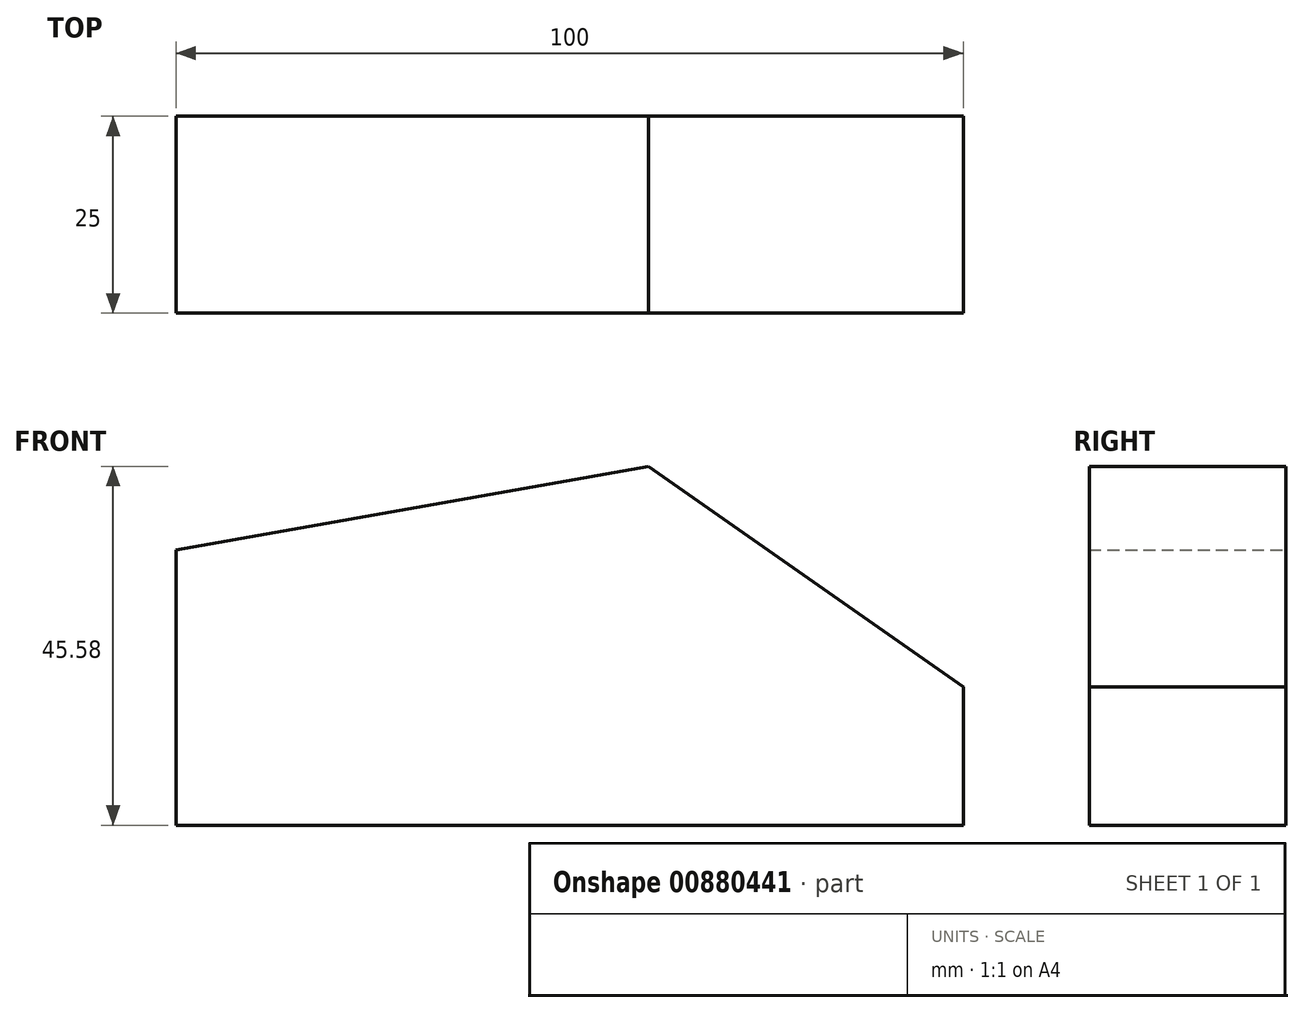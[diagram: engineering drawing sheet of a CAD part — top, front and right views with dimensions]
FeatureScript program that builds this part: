
annotation { "Feature Type Name" : "Feature", "Feature Type Description" : "" }
export const myFeature = defineFeature(function(context is Context, id is Id, definition is map)
    precondition{}
    {
        {
            var Q0;
            Q0=qCreatedBy(makeId("Front.planeOp"),FACE);
            var sketch = newSketch(context, id + "F0", { "sketchPlane" : qUnion([Q0])});
            skLineSegment(sketch, "E0", {"start": v(0, 0) * mm, "end": v(100, 0) * mm});
            skLineSegment(sketch, "E1", {"start": v(100, 0) * mm, "end": v(100, 17.57) * mm});
            skLineSegment(sketch, "E2", {"start": v(100, 17.57) * mm, "end": v(60, 45.58) * mm});
            skLineSegment(sketch, "E3", {"start": v(60, 45.58) * mm, "end": v(0, 35) * mm});
            skLineSegment(sketch, "E4", {"start": v(0, 35) * mm, "end": v(0, 0) * mm});
            skSolve(sketch);
        }
        {
            var Q0;
            Q0=makeQuery(id+"F0.imprint","IMPRINT",FACE,{"disambiguationData":[TD([[makeQuery(id+"F0.imprint","IMPRINT",EDGE,{"derivedFrom":sQuery(id+"F0.wireOp",EDGE,"E0")}),1.0]])]});
            extrude(context, id + "F1", {"entities" : qUnion([Q0]), "depth" : 25 * mm, "offsetDistance" : 25 * mm});
        }
    });
